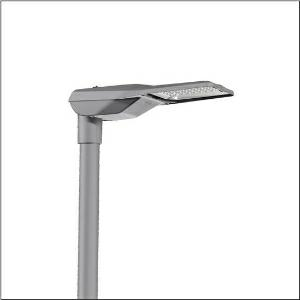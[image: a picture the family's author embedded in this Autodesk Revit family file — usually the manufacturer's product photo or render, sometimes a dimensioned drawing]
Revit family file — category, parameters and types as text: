
# Revit family: streetlight_sl_21_mini___p0_5a_5xe2v33s08gb_4fda
name_source: partatom
category: Lighting Fixtures
units: mm (PartAtom-declared; Revit-internal decimal feet)

## family parameters
Cut with Voids When Loaded = No
Host = Face
Light Source = No
Part Type = Normal
Room Calculation Point = No
Round Connector Dimension = Use Diameter
Shared = No

## types (1)
- --- (1 x LED, 5840 lm, 40.4 W, 3000K)
    Apparent Load = 40 VA
    CIE Flux Codes = 37 73 96 100 100
    Color Rendering = 70
    Color Temperature = 3000K
    Default Elevation = 1800 mm
    Description = Streetlight SL 21 mini, mast luminaire, primary light control with lens, of PMMA, primary optical cover: cover, of toughened safety glass, transparent, light distribution: P0.5a, light emission: direct distribution, primary light characteristic: asymmetric, installation type: post-top, side-entry, LED, High Power LED, rated luminous flux: 5.840lm, luminous efficacy: 145lm/W, light colour: 730, colour temperature: 3000K, control gear: D4i, control: pre-setting: logarithmic dimming characteristic, flexible luminous flux parameterisation, time-dependent luminous flux control, constant luminous flux control, overheat protection, mains connection: 220..240V, AC, 50/60Hz, start of lifetime: 40W, end of service life: 41W, reduction: 19W, luminaire housing, of diecast aluminium, powder-coated, SITECO metallic grey (DB 702S), corrosivity category C5 high according to DIN EN ISO 12944, multi-level sealing system, sealing non-destructively replaceable, inclination adjustable: 0°, 5°, 10°, 15°, please order mast flange separately, length: 628mm, width: 235mm, height: 110mm, mast flange for spigot size: 42mm (side-entry): 5XC10008XM4, 60/48mm (side-entry/post-top): 5XC10108XM2, 76/60mm (side-entry/post-top): 5XC10108XM1, mounting height: 4..8m, Smart Interface above, protection rating (complete): IP66, insulation class (complete): insulation class II (safety insulation), certification: CE, ENEC, ENEC+, VDE, impact resistance: IK10, permissible operating ambient temperature for outdoor applications: -40..+50°C, standard-compliant lighting for roads and squares, packaging unit: 1 piece

Light Distribution: P0.5a
    Height = 110 mm
    Lamp = 1 x LED
    Lamp Light Flux = 5840 lm
    Lamp Power = 40.4 W
    Lamp count = 1
    Length = 625 mm
    Luminous efficacy = 145 lm/W
    Manufacturer = Siteco
    ModVariant = No
    Model = 5XE2V33S08GB
    Number of Poles = 1
    OnlyDefault = Yes
    Power Factor = 1
    Product Name = Streetlight SL 21 mini | P0.5a
    Product group = mast luminaire | pylon top
    ProductGroupID = 6100
    Protection Class = Protection class II
    Protection Degree = IP 66
    RLX_Detail_Level = 1
    RLX_Emergency_Light_Flux = 0 lm
    RLX_Emergency_Type = 0
    RLX_Emergency_Type_DB = No
    RlxData = <blob elided: 91765 chars, md5=eb51c49e>
    Socket = socket
    Standby Power = 0 W
    System Light Flux = 5840 lm
    System Power = 40 W
    Type Comments = factory setting: luminous flux: 100 % | dim-lin: 254 | 812 mA
    Type Image = l_1003515.jpg
    URL = http://relux.com
    VarID = @adj_077281
    Voltage = 0 V
    Weight = 0.00 kg
    Width = 234 mm

## geometry (parser evidence)
native form markers: Blend x4, Sweep x13
no freeform markers — native parametric forms only
